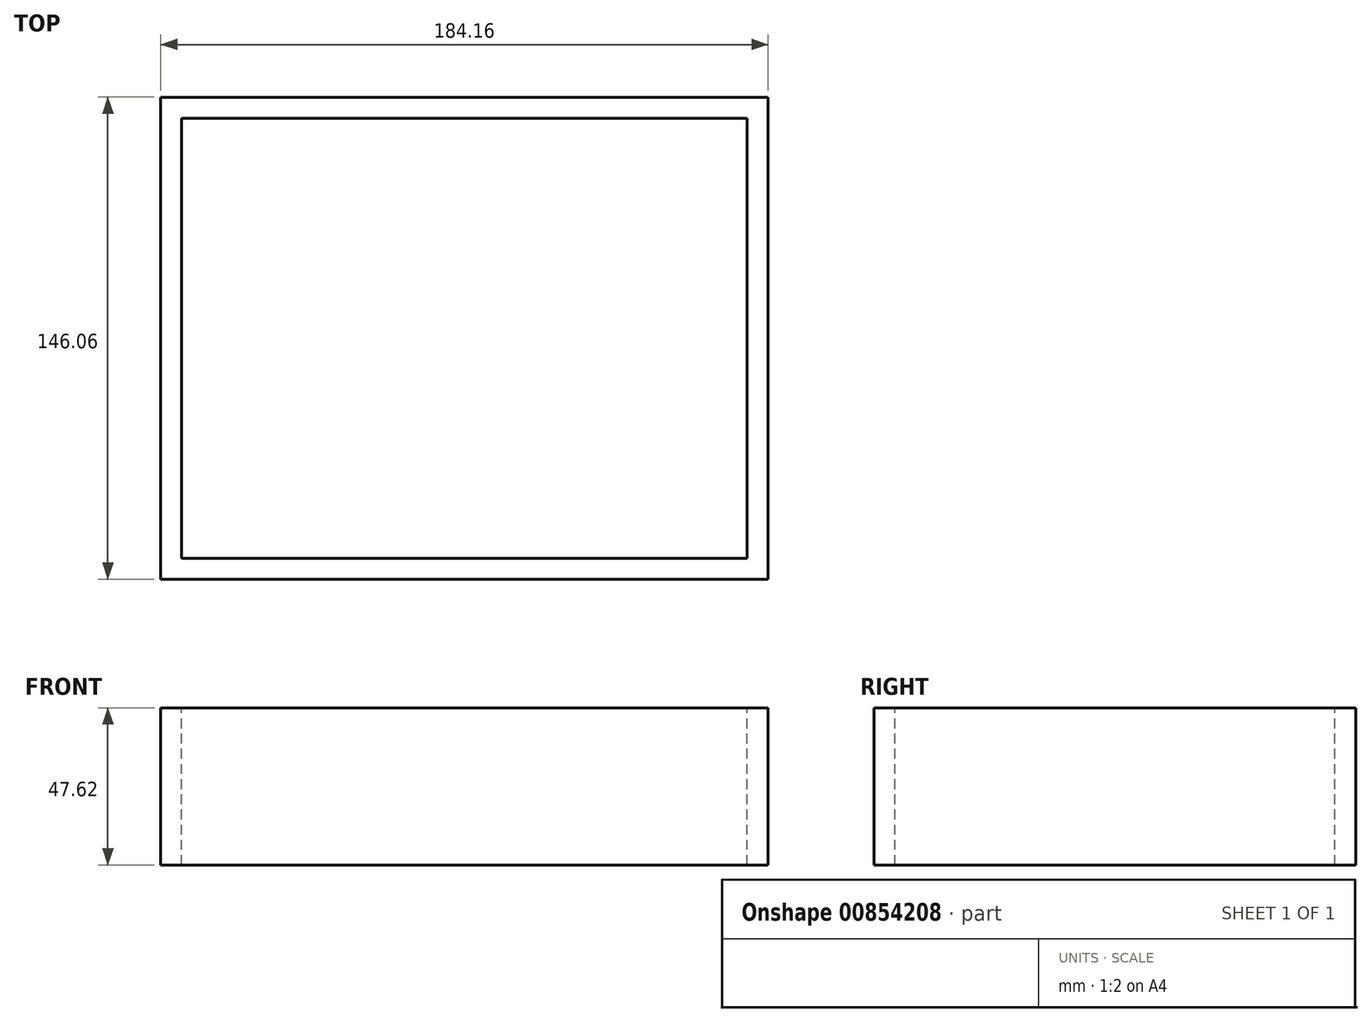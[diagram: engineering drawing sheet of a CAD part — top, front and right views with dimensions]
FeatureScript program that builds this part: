
annotation { "Feature Type Name" : "Feature", "Feature Type Description" : "" }
export const myFeature = defineFeature(function(context is Context, id is Id, definition is map)
    precondition{}
    {
        {
            var Q0;
            Q0=qCreatedBy(makeId("Top.planeOp"),FACE);
            var sketch = newSketch(context, id + "F0", { "sketchPlane" : qUnion([Q0])});
            skLineSegment(sketch, "E0.bottom", {"start": v(85.72, -66.68) * mm, "end": v(-85.73, -66.67) * mm});
            skLineSegment(sketch, "E0.top", {"start": v(85.73, 66.67) * mm, "end": v(-85.72, 66.68) * mm});
            skLineSegment(sketch, "E0.left", {"start": v(85.72, -66.68) * mm, "end": v(85.73, 66.67) * mm});
            skLineSegment(sketch, "E0.right", {"start": v(-85.73, -66.67) * mm, "end": v(-85.72, 66.68) * mm});
            skPoint(sketch, "E0.middle", {"position": v(0, 0) * mm});
            skLineSegment(sketch, "E1.0", {"start": v(85.73, 66.68) * mm, "end": v(-85.73, 66.68) * mm});
            skLineSegment(sketch, "E1.1", {"start": v(85.73, -66.68) * mm, "end": v(85.73, 66.68) * mm});
            skLineSegment(sketch, "E1.2", {"start": v(85.73, -66.68) * mm, "end": v(-85.73, -66.68) * mm});
            skLineSegment(sketch, "E1.3", {"start": v(-85.73, -66.68) * mm, "end": v(-85.73, 66.68) * mm});
            skLineSegment(sketch, "E2.0", {"start": v(92.08, 73.02) * mm, "end": v(-92.07, 73.03) * mm});
            skLineSegment(sketch, "E2.1", {"start": v(92.07, -73.03) * mm, "end": v(92.08, 73.02) * mm});
            skLineSegment(sketch, "E2.2", {"start": v(92.07, -73.03) * mm, "end": v(-92.08, -73.02) * mm});
            skLineSegment(sketch, "E2.3", {"start": v(-92.08, -73.03) * mm, "end": v(-92.07, 73.03) * mm});
            skLineSegment(sketch, "E3", {"start": v(-85.72, 66.68) * mm, "end": v(-85.72, 69.22) * mm});
            skLineSegment(sketch, "E4", {"start": v(-85.73, 69.22) * mm, "end": v(-92.08, 69.22) * mm});
            skLineSegment(sketch, "E5", {"start": v(85.73, 66.67) * mm, "end": v(85.73, 69.22) * mm});
            skLineSegment(sketch, "E6", {"start": v(85.73, 69.22) * mm, "end": v(92.08, 69.22) * mm});
            skLineSegment(sketch, "E7", {"start": v(-85.73, -66.67) * mm, "end": v(-85.73, -69.22) * mm});
            skLineSegment(sketch, "E8", {"start": v(-85.73, -69.22) * mm, "end": v(-92.08, -69.22) * mm});
            skLineSegment(sketch, "E9", {"start": v(85.72, -66.68) * mm, "end": v(85.72, -69.21) * mm});
            skLineSegment(sketch, "E10", {"start": v(85.73, -69.21) * mm, "end": v(92.08, -69.21) * mm});
            skSolve(sketch);
        }
        {
            var Q0;
            Q0=sQuery(id+"F0.wireOp",EDGE,"E2.0");
            var Q1;
            Q1=sQuery(id+"F0.wireOp",EDGE,"E2.3");
            var Q2;
            Q2=sQuery(id+"F0.wireOp",EDGE,"E2.2");
            var Q3;
            Q3=sQuery(id+"F0.wireOp",EDGE,"E2.1");
            var Q4;
            Q4=sQuery(id+"F0.wireOp",EDGE,"E0.left");
            var Q5;
            Q5=sQuery(id+"F0.wireOp",EDGE,"E0.bottom");
            var Q6;
            Q6=sQuery(id+"F0.wireOp",EDGE,"E1.3");
            var Q7;
            Q7=sQuery(id+"F0.wireOp",EDGE,"E0.top");
            extrude(context, id + "F1", {"bodyType" : ToolBodyType.SURFACE, "surfaceEntities" : qUnion([Q0, Q1, Q2, Q3, Q4, Q5, Q6, Q7]), "depth" : 47.62 * mm, "offsetDistance" : 25.4 * mm});
        }
    });
